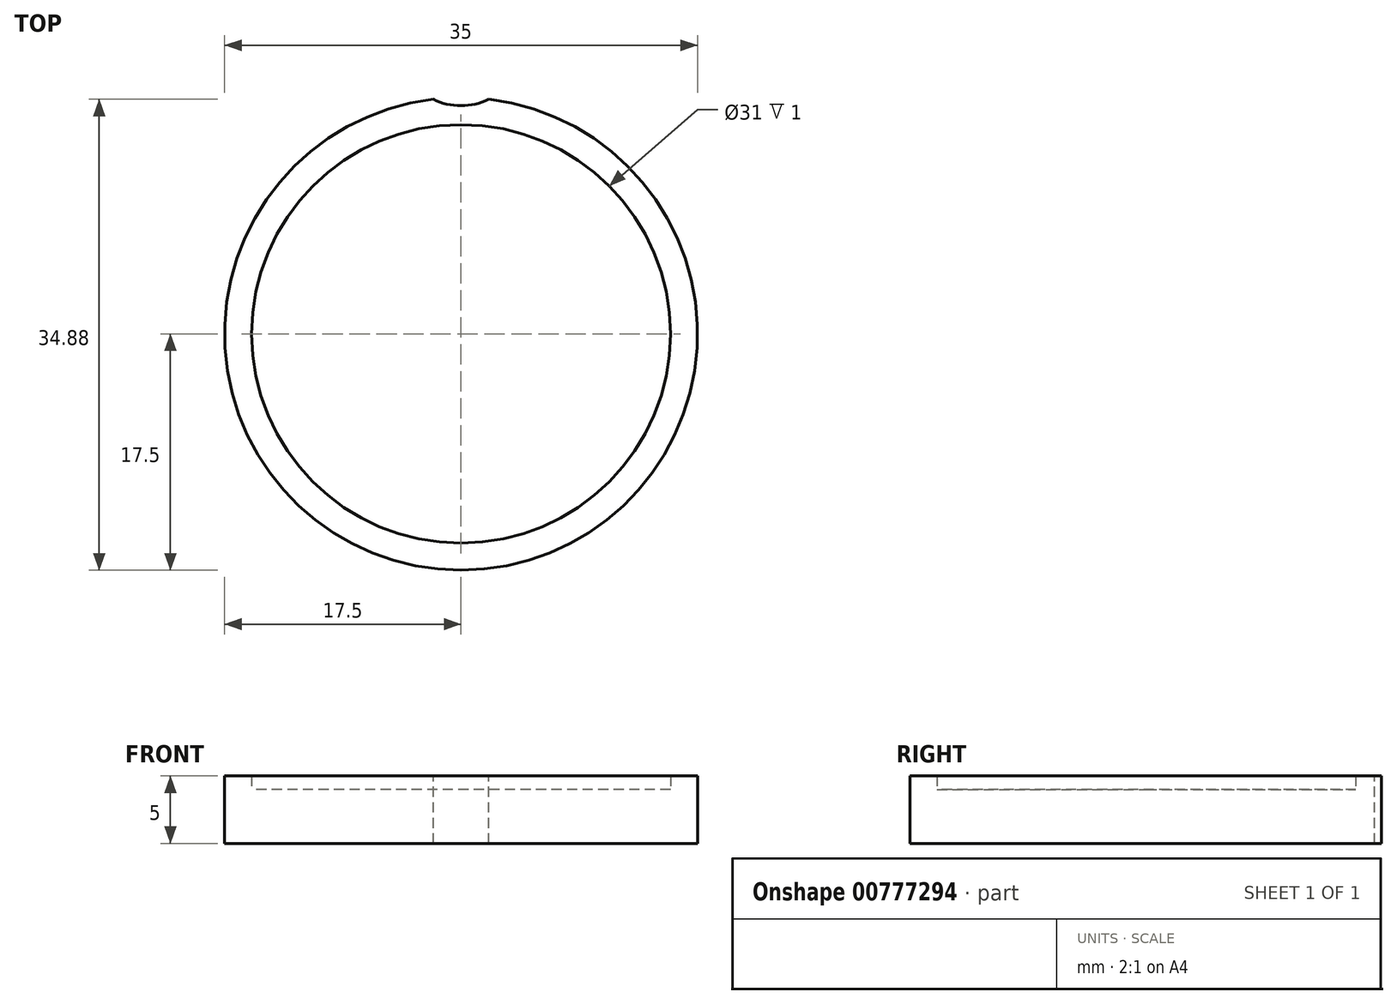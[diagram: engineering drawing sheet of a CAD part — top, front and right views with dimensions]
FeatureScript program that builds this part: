
annotation { "Feature Type Name" : "Feature", "Feature Type Description" : "" }
export const myFeature = defineFeature(function(context is Context, id is Id, definition is map)
    precondition{}
    {
        {
            var Q0;
            Q0=qCreatedBy(makeId("Top.planeOp"),FACE);
            var sketch = newSketch(context, id + "F0", { "sketchPlane" : qUnion([Q0])});
            skCircle(sketch, "E0", {"center": v(0, 0) * mm, "radius": 17.5 * mm});
            skSolve(sketch);
        }
        {
            var Q0;
            Q0 = qSketchRegion(id + "F0", true);
            extrude(context, id + "F1", {"entities" : qUnion([Q0]), "depth" : 4 * mm, "offsetDistance" : 25 * mm});
        }
        {
            var Q0;
            Q0=makeQuery(id+"F1.opExtrude","CAP_FACE",FACE,{"disambiguationData":[OSD([sQuery(id+"F0.wireOp",EDGE,"E0")])],"isStart":false});
            var sketch = newSketch(context, id + "F2", { "sketchPlane" : qUnion([Q0])});
            skCircle(sketch, "E1.0", {"center": v(0, 0) * mm, "radius": 15.5 * mm});
            skSolve(sketch);
        }
        {
            var Q0;
            Q0=makeQuery(id+"F2.imprint","IMPRINT",FACE,{"disambiguationData":[TD([[makeQuery(id+"F2.imprint","IMPRINT",EDGE,{"derivedFrom":sQuery(id+"F2.wireOp",EDGE,"E1.0")}),-1.0]])]});
            extrude(context, id + "F3", {"entities" : qUnion([Q0]), "operationType" : NewBodyOperationType.ADD, "depth" : 1 * mm, "offsetDistance" : 25 * mm});
        }
        {
            var Q0;
            Q0=makeQuery(id+"F3.opExtrude","CAP_FACE",FACE,{"disambiguationData":[OSD([sQuery(id+"F0.wireOp",EDGE,"E0"),sQuery(id+"F2.wireOp",EDGE,"E1.0")])],"isStart":false});
            var sketch = newSketch(context, id + "F4", { "sketchPlane" : qUnion([Q0])});
            skCircle(sketch, "E2", {"center": v(0, 21.54) * mm, "radius": 4.64 * mm});
            skSolve(sketch);
        }
        {
            var Q0;
            Q0=makeQuery(id+"F4.imprint","IMPRINT",FACE,{"disambiguationData":[TD([[makeQuery(id+"F4.imprint","IMPRINT",EDGE,{"derivedFrom":makeQuery(id+"F3.opExtrude","CAP_EDGE",EDGE,{"disambiguationData":[OSD([sQuery(id+"F2.wireOp",EDGE,"E1.0")])],"isStart":false})}),-1.0]])]});
            var Q1;
            Q1=makeQuery(id+"F4.imprint","IMPRINT",FACE,{"disambiguationData":[TD([[makeQuery(id+"F4.imprint","IMPRINT",EDGE,{"derivedFrom":makeQuery(id+"F3.opExtrude","CAP_EDGE",EDGE,{"disambiguationData":[OSD([sQuery(id+"F2.wireOp",EDGE,"E1.0")])],"isStart":false})}),1.0]])]});
            extrude(context, id + "F5", {"entities" : qUnion([Q0, Q1]), "operationType" : NewBodyOperationType.INTERSECT, "oppositeDirection" : true, "depth" : 25 * mm, "offsetDistance" : 25 * mm});
        }
    });
